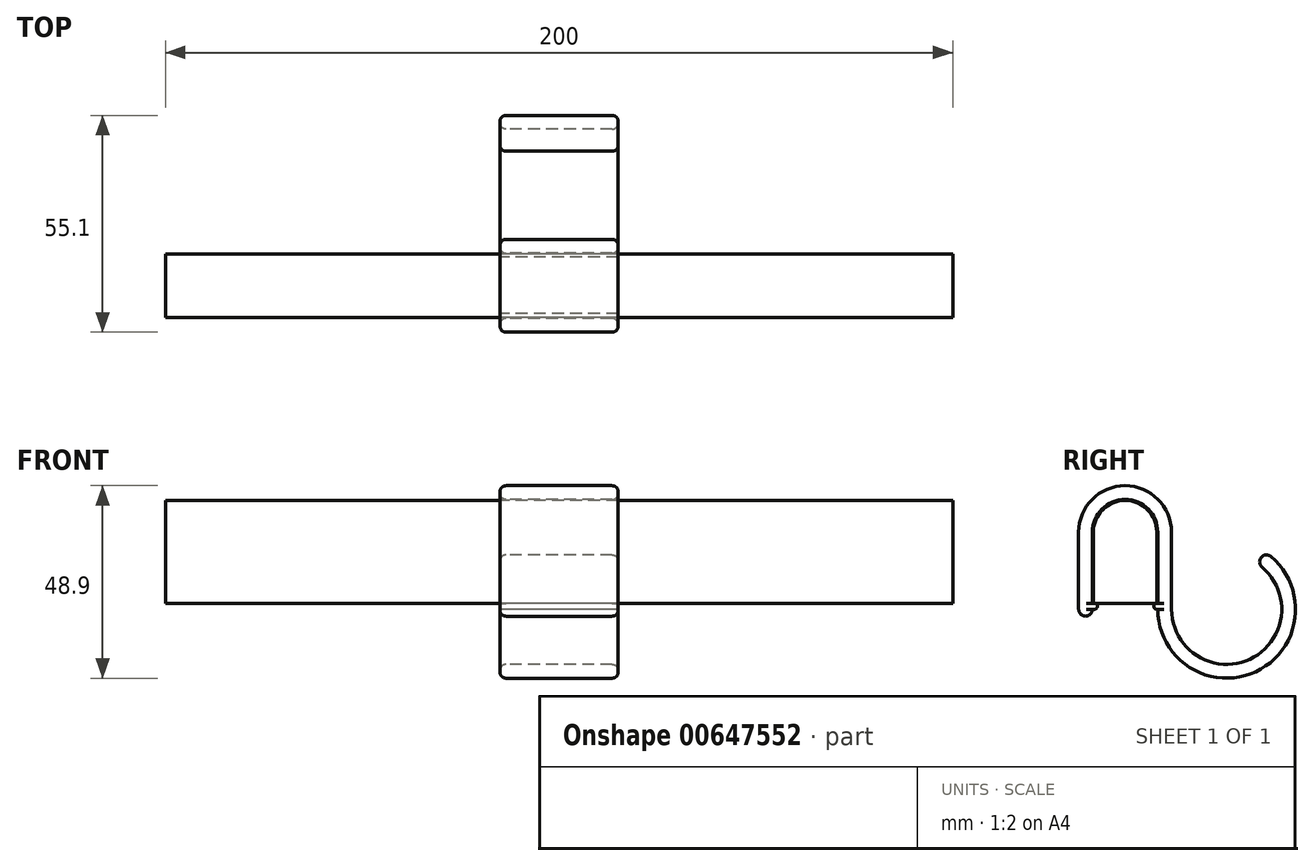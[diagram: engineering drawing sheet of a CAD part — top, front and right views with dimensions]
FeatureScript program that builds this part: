
annotation { "Feature Type Name" : "Feature", "Feature Type Description" : "" }
export const myFeature = defineFeature(function(context is Context, id is Id, definition is map)
    precondition{}
    {
        {
            var Q0;
            Q0=qCreatedBy(makeId("Right.planeOp"),FACE);
            var sketch = newSketch(context, id + "F0", { "sketchPlane" : qUnion([Q0])});
            skArc(sketch, "E0", {"start": v(8.05, 0) * mm, "mid": v(0, 8.05) * mm, "end": v(-8.05, 0) * mm});
            skLineSegment(sketch, "E1", {"start": v(-8.05, 0) * mm, "end": v(-8.05, -18.1) * mm});
            skLineSegment(sketch, "E2", {"start": v(8.05, 0) * mm, "end": v(8.05, -18.1) * mm});
            skLineSegment(sketch, "E3", {"start": v(-8.05, -18.1) * mm, "end": v(8.05, -18.1) * mm});
            skSolve(sketch);
        }
        {
            var Q0;
            Q0=makeQuery(id+"F0.imprint","IMPRINT",FACE,{"disambiguationData":[TD([[makeQuery(id+"F0.imprint","IMPRINT",EDGE,{"derivedFrom":sQuery(id+"F0.wireOp",EDGE,"E0")}),1.0]])]});
            extrude(context, id + "F1", {"entities" : qUnion([Q0]), "endBound" : BoundingType.SYMMETRIC, "depth" : 200 * mm, "offsetDistance" : 25 * mm});
        }
        {
            var Q0;
            Q0=qCreatedBy(makeId("Right.planeOp"),FACE);
            var sketch = newSketch(context, id + "F2", { "sketchPlane" : qUnion([Q0])});
            skLineSegment(sketch, "E4.0", {"start": v(-8.05, 0) * mm, "end": v(-8.05, -18.1) * mm});
            skArc(sketch, "E5.0", {"start": v(8.05, 0) * mm, "mid": v(0, 8.05) * mm, "end": v(-8.05, 0) * mm});
            skLineSegment(sketch, "E6.0", {"start": v(8.05, 0) * mm, "end": v(8.05, -18.1) * mm});
            skLineSegment(sketch, "E7.0", {"start": v(-8.05, -18.1) * mm, "end": v(8.05, -18.1) * mm});
            skArc(sketch, "E8.0", {"start": v(8.3, 0) * mm, "mid": v(0, 8.3) * mm, "end": v(-8.3, 0) * mm});
            skLineSegment(sketch, "E8.1", {"start": v(8.3, 0) * mm, "end": v(8.3, -19.6) * mm});
            skLineSegment(sketch, "E8.3", {"start": v(-8.3, 0) * mm, "end": v(-8.3, -19.6) * mm});
            skArc(sketch, "E9.0", {"start": v(11.8, 0) * mm, "mid": v(0, 11.8) * mm, "end": v(-11.8, 0) * mm});
            skLineSegment(sketch, "E9.1", {"start": v(11.8, 0) * mm, "end": v(11.8, -19.6) * mm});
            skLineSegment(sketch, "E9.2", {"start": v(-11.8, -19.6) * mm, "end": v(-8.3, -19.6) * mm});
            skLineSegment(sketch, "E9.3", {"start": v(-11.8, 0) * mm, "end": v(-11.8, -19.6) * mm});
            skLineSegment(sketch, "E10.trimOffspring", {"start": v(8.3, -19.6) * mm, "end": v(11.8, -19.6) * mm});
            skLineSegment(sketch, "E11", {"start": v(-8.3, -18.1) * mm, "end": v(-7.8, -18.1) * mm});
            skLineSegment(sketch, "E12", {"start": v(-7.8, -19.6) * mm, "end": v(-8.3, -19.6) * mm});
            skArc(sketch, "E13", {"start": v(-7.8, -19.6) * mm, "mid": v(-7.05, -18.85) * mm, "end": v(-7.8, -18.1) * mm});
            skLineSegment(sketch, "E14", {"start": v(8.3, -19.6) * mm, "end": v(8.05, -19.6) * mm});
            skLineSegment(sketch, "E15", {"start": v(8.05, -18.1) * mm, "end": v(8.3, -18.1) * mm});
            skArc(sketch, "E16", {"start": v(8.05, -18.1) * mm, "mid": v(7.3, -18.85) * mm, "end": v(8.05, -19.6) * mm});
            skArc(sketch, "E17", {"start": v(11.8, -19.6) * mm, "mid": v(31.72, -32.29) * mm, "end": v(34.8, -8.88) * mm});
            skArc(sketch, "E18", {"start": v(8.3, -19.6) * mm, "mid": v(33.2, -35.46) * mm, "end": v(37.05, -6.2) * mm});
            skLineSegment(sketch, "E19", {"start": v(25.8, -19.6) * mm, "end": v(38.2, -19.6) * mm, "construction": true});
            skLineSegment(sketch, "E20", {"start": v(34.8, -8.88) * mm, "end": v(37.05, -6.2) * mm, "construction": true});
            skArc(sketch, "E21", {"start": v(34.8, -8.88) * mm, "mid": v(34.58, -6.4) * mm, "end": v(37.05, -6.2) * mm});
            skArc(sketch, "E22", {"start": v(-11.8, -19.6) * mm, "mid": v(-10.05, -21.35) * mm, "end": v(-8.3, -19.6) * mm});
            skSolve(sketch);
        }
        {
            var Q0;
            {var subQ1=sQuery(id+"F2.wireOp",EDGE,"E8.0");Q0=makeQuery(id+"F2.imprint","IMPRINT",FACE,{"disambiguationData":[TD([[makeQuery(id+"F2.imprint","IMPRINT",EDGE,{"derivedFrom":subQ1}),-1.0]])]});}
            var Q1;
            Q1=makeQuery(id+"F2.imprint","IMPRINT",FACE,{"disambiguationData":[TD([[makeQuery(id+"F2.imprint","IMPRINT",EDGE,{"derivedFrom":sQuery(id+"F2.wireOp",EDGE,"E10.trimOffspring")}),-1.0]])]});
            var Q2;
            {var subQ0=sQuery(id+"F2.wireOp",EDGE,"E14");Q2=makeQuery(id+"F2.imprint","IMPRINT",FACE,{"disambiguationData":[TD([[makeQuery(id+"F2.imprint","IMPRINT",EDGE,{"derivedFrom":subQ0}),-1.0]])]});}
            var Q3;
            Q3=makeQuery(id+"F2.imprint","IMPRINT",FACE,{"disambiguationData":[TD([[makeQuery(id+"F2.imprint","IMPRINT",EDGE,{"derivedFrom":sQuery(id+"F2.wireOp",EDGE,"E9.2")}),-1.0]])]});
            var Q4;
            {var subQ2=sQuery(id+"F2.wireOp",EDGE,"E11");Q4=makeQuery(id+"F2.imprint","IMPRINT",FACE,{"disambiguationData":[TD([[makeQuery(id+"F2.imprint","IMPRINT",EDGE,{"derivedFrom":subQ2}),-1.0]])]});}
            extrude(context, id + "F3", {"entities" : qUnion([Q0, Q1, Q2, Q3, Q4]), "endBound" : BoundingType.SYMMETRIC, "depth" : 30 * mm, "offsetDistance" : 25 * mm});
        }
        {
            var Q0;
            Q0=makeQuery(id+"F3.opExtrude","CAP_EDGE",EDGE,{"disambiguationData":[OSD([sQuery(id+"F2.wireOp",EDGE,"E17")])],"isStart":false});
            var Q1;
            Q1=makeQuery(id+"F3.opExtrude","CAP_EDGE",EDGE,{"disambiguationData":[OSD([sQuery(id+"F2.wireOp",EDGE,"E8.3")])],"isStart":false});
            var Q2;
            Q2=makeQuery(id+"F3.opExtrude","CAP_EDGE",EDGE,{"disambiguationData":[OSD([sQuery(id+"F2.wireOp",EDGE,"E9.3")])],"isStart":true});
            var Q3;
            Q3=makeQuery(id+"F3.opExtrude","CAP_EDGE",EDGE,{"disambiguationData":[OSD([sQuery(id+"F2.wireOp",EDGE,"E8.3")])],"isStart":true});
            fillet(context, id + "F4", {"entities" : qUnion([Q0, Q1, Q2, Q3]), "tangentPropagation" : true, "radius" : 1.5 * mm, "defaultsChanged" : false, "vertexSettings" : [], "allowEdgeOverflow" : false});
        }
    });
